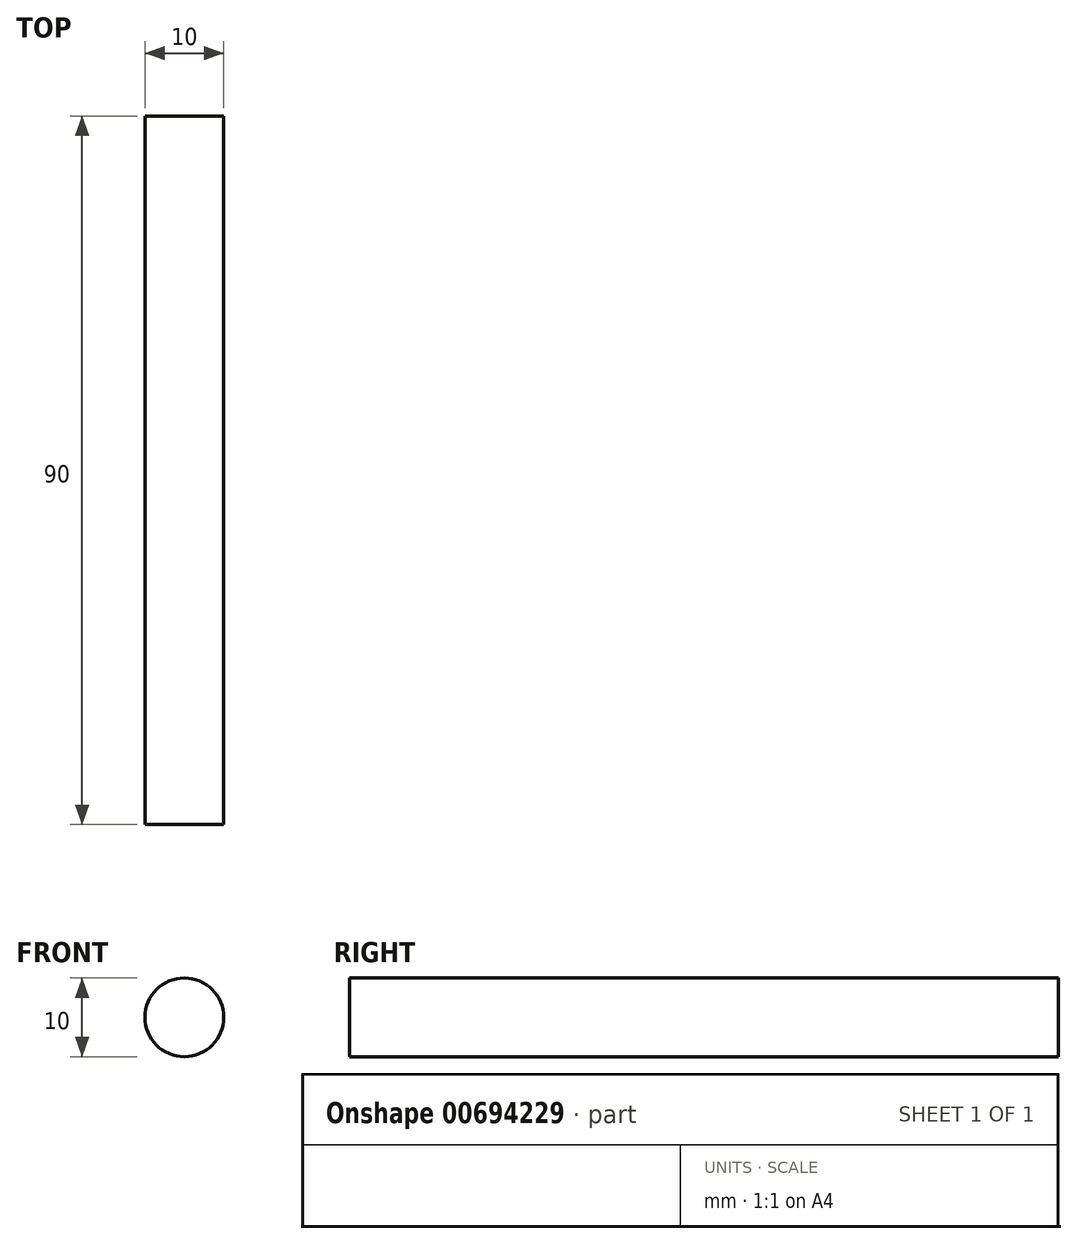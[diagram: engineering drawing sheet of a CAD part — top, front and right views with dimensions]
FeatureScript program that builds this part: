
annotation { "Feature Type Name" : "Feature", "Feature Type Description" : "" }
export const myFeature = defineFeature(function(context is Context, id is Id, definition is map)
    precondition{}
    {
        {
            var Q0;
            Q0=qCreatedBy(makeId("Front.planeOp"),FACE);
            var sketch = newSketch(context, id + "F0", { "sketchPlane" : qUnion([Q0])});
            skCircle(sketch, "E0", {"center": v(0, 0) * mm, "radius": 5 * mm});
            skCircle(sketch, "E1", {"center": v(0, 0) * mm, "radius": 13.87 * mm});
            skSolve(sketch);
        }
        {
            var Q0;
            Q0=makeQuery(id+"F0.imprint","IMPRINT",FACE,{"disambiguationData":[TD([[makeQuery(id+"F0.imprint","IMPRINT",EDGE,{"derivedFrom":sQuery(id+"F0.wireOp",EDGE,"E0")}),1.0]])]});
            extrude(context, id + "F1", {"entities" : qUnion([Q0]), "endBound" : BoundingType.SYMMETRIC, "depth" : 90 * mm, "offsetDistance" : 25 * mm});
        }
    });
